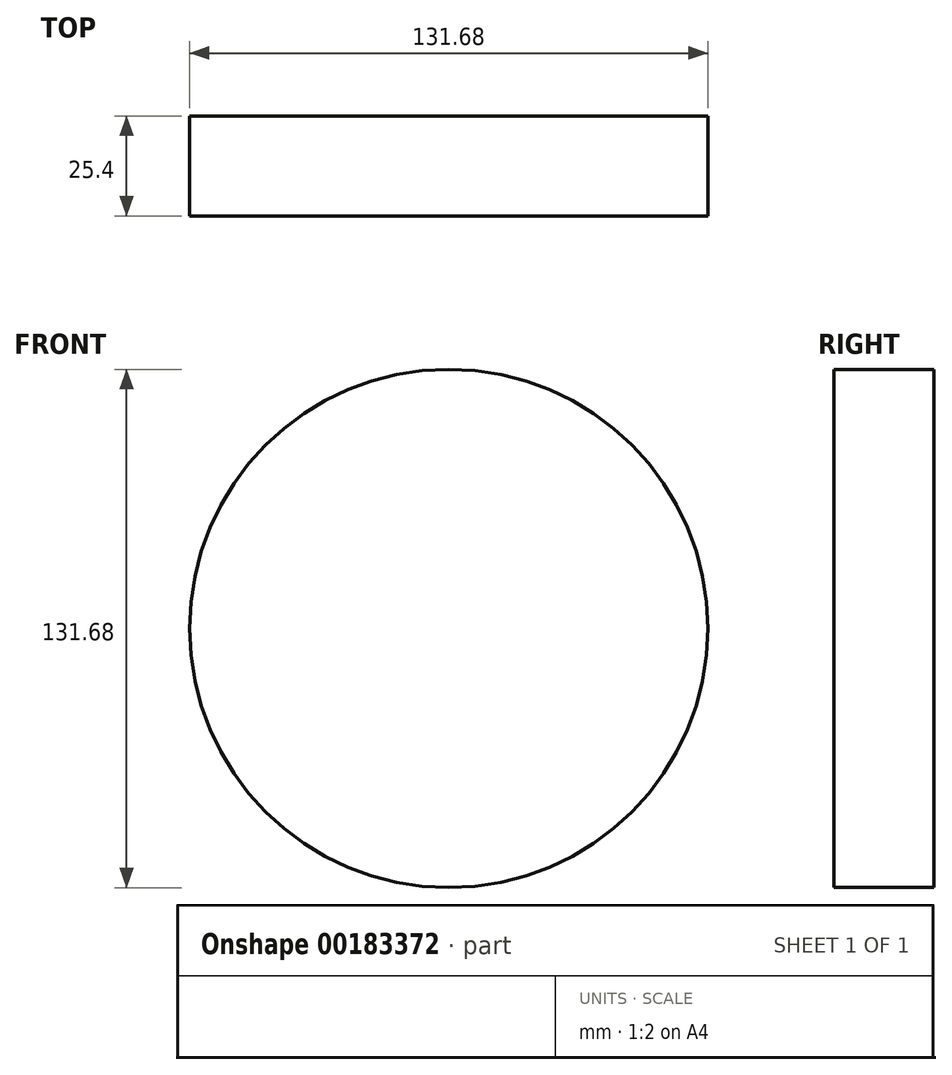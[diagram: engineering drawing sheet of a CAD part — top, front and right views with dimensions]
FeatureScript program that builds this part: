
annotation { "Feature Type Name" : "Feature", "Feature Type Description" : "" }
export const myFeature = defineFeature(function(context is Context, id is Id, definition is map)
    precondition{}
    {
        {
            var Q0;
            Q0=qCreatedBy(makeId("Front.planeOp"),FACE);
            var sketch = newSketch(context, id + "F0", { "sketchPlane" : qUnion([Q0])});
            skCircle(sketch, "E0", {"center": v(0, 0) * mm, "radius": 65.84 * mm});
            skSolve(sketch);
        }
        {
            var Q0;
            Q0=makeQuery(id+"F0.imprint","IMPRINT",FACE,{"disambiguationData":[TD([[makeQuery(id+"F0.imprint","IMPRINT",EDGE,{"derivedFrom":sQuery(id+"F0.wireOp",EDGE,"E0")}),1.0]])]});
            extrude(context, id + "F1", {"entities" : qUnion([Q0]), "depth" : 25.4 * mm});
        }
    });
